# Revit family: 7344 Blanco Adj Twin
name_source: partatom
category: Lighting Fixtures
revit_build: Autodesk Revit 2018 (Build: 20170223_1515(x64)
units: mm (PartAtom-declared; Revit-internal decimal feet)

## family parameters
Always vertical = Yes
Cut with Voids When Loaded = No
Host = Ceiling
Light Source = No
OmniClass Number = 23.80.70.11
OmniClass Title = Luminaries for Internal Lighting
Part Type = Normal
Room Calculation Point = No
Round Connector Dimension = Use Diameter
Shared = No

## types (1)
- CE
    Dimmable = Yes
    Dimming Method = Lamp Dependant
    Driver Included = Not Applicable
    Driver Required = No
    Efficacy (lm/w) = Lamp Dependant
    Electrical Class = 1
    Lamp = GU10 - LED
    Light Source Fixed = No
    Location Rating = IP20
    Main Finish = Plaster
    Main Material = Plaster
    Power (Watts) = 2x 6W MAX
    Product Location = Indoor
    Product Name = Blanco Twin Adjustable
    Product SKU = 1253006

## geometry (parser evidence)
native form markers: Sweep x2
no freeform markers — native parametric forms only
